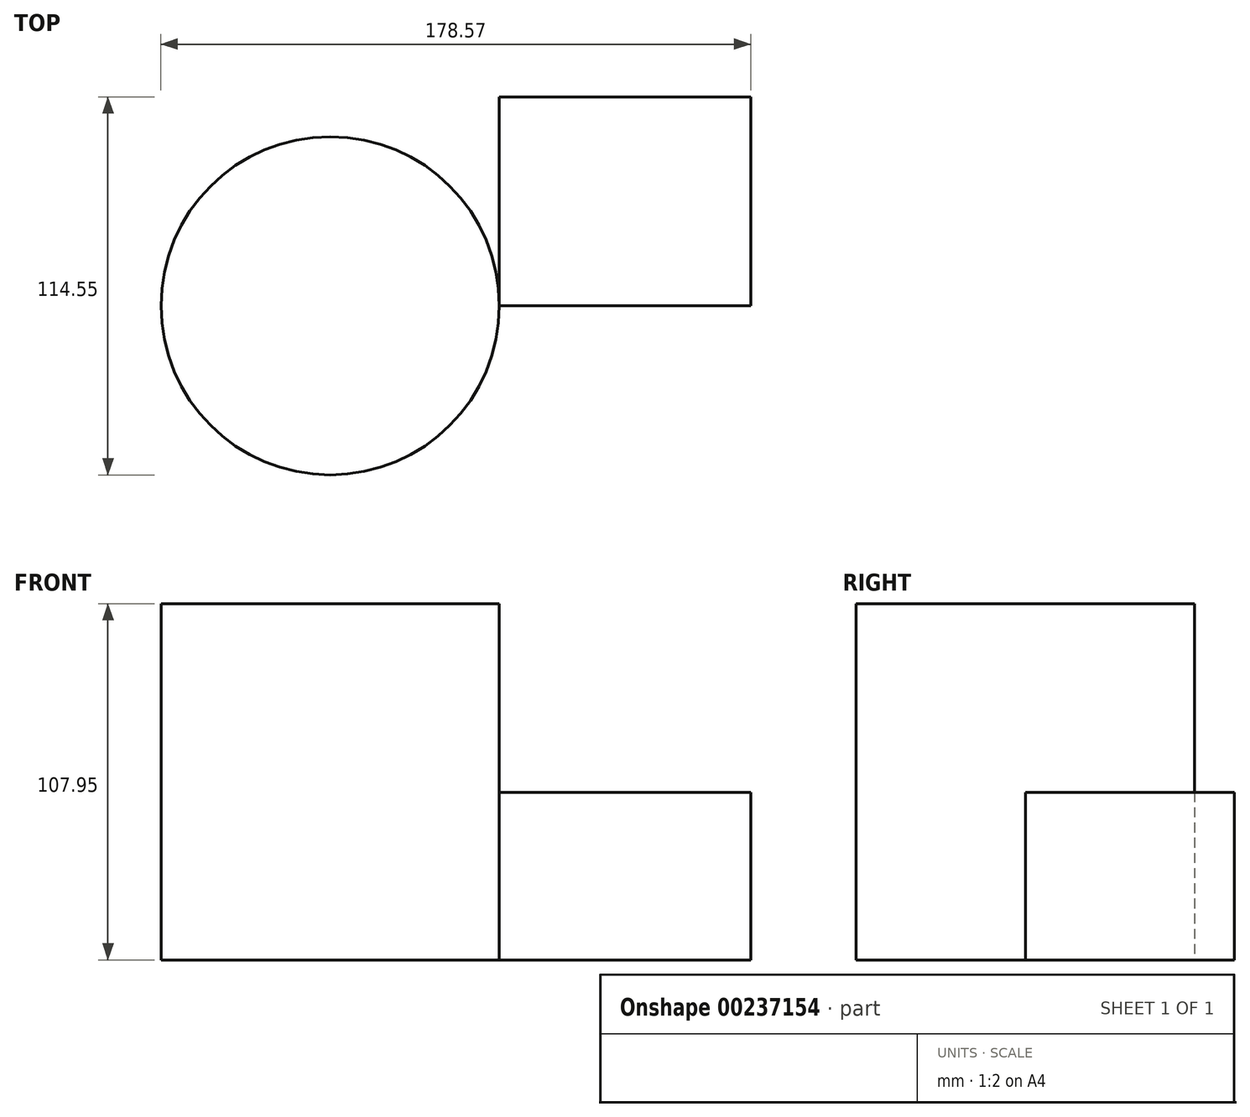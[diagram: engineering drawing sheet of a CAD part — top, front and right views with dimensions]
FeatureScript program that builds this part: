
annotation { "Feature Type Name" : "Feature", "Feature Type Description" : "" }
export const myFeature = defineFeature(function(context is Context, id is Id, definition is map)
    precondition{}
    {
        {
            var Q0;
            Q0=qCreatedBy(makeId("Top.planeOp"),FACE);
            var sketch = newSketch(context, id + "F0", { "sketchPlane" : qUnion([Q0])});
            skCircle(sketch, "E0", {"center": v(-51.24, 0) * mm, "radius": 51.24 * mm});
            skSolve(sketch);
        }
        {
            var Q0;
            Q0=makeQuery(id+"F0.imprint","IMPRINT",FACE,{"disambiguationData":[TD([[makeQuery(id+"F0.imprint","IMPRINT",EDGE,{"derivedFrom":sQuery(id+"F0.wireOp",EDGE,"E0")}),1.0]])]});
            extrude(context, id + "F1", {"entities" : qUnion([Q0]), "depth" : 107.95 * mm});
        }
        {
            var Q0;
            Q0=qCreatedBy(makeId("Top.planeOp"),FACE);
            var sketch = newSketch(context, id + "F2", { "sketchPlane" : qUnion([Q0])});
            skLineSegment(sketch, "E1.bottom", {"start": v(76.08, 0) * mm, "end": v(0, 0) * mm});
            skLineSegment(sketch, "E1.top", {"start": v(76.08, 63.3) * mm, "end": v(0, 63.3) * mm});
            skLineSegment(sketch, "E1.left", {"start": v(76.08, 0) * mm, "end": v(76.08, 63.3) * mm});
            skLineSegment(sketch, "E1.right", {"start": v(0, 0) * mm, "end": v(0, 63.3) * mm});
            skSolve(sketch);
        }
        {
            var Q0;
            Q0=makeQuery(id+"F2.imprint","IMPRINT",FACE,{"disambiguationData":[TD([[makeQuery(id+"F2.imprint","IMPRINT",EDGE,{"derivedFrom":sQuery(id+"F2.wireOp",EDGE,"E1.bottom")}),-1.0]])]});
            extrude(context, id + "F3", {"entities" : qUnion([Q0]), "depth" : 50.8 * mm});
        }
    });
